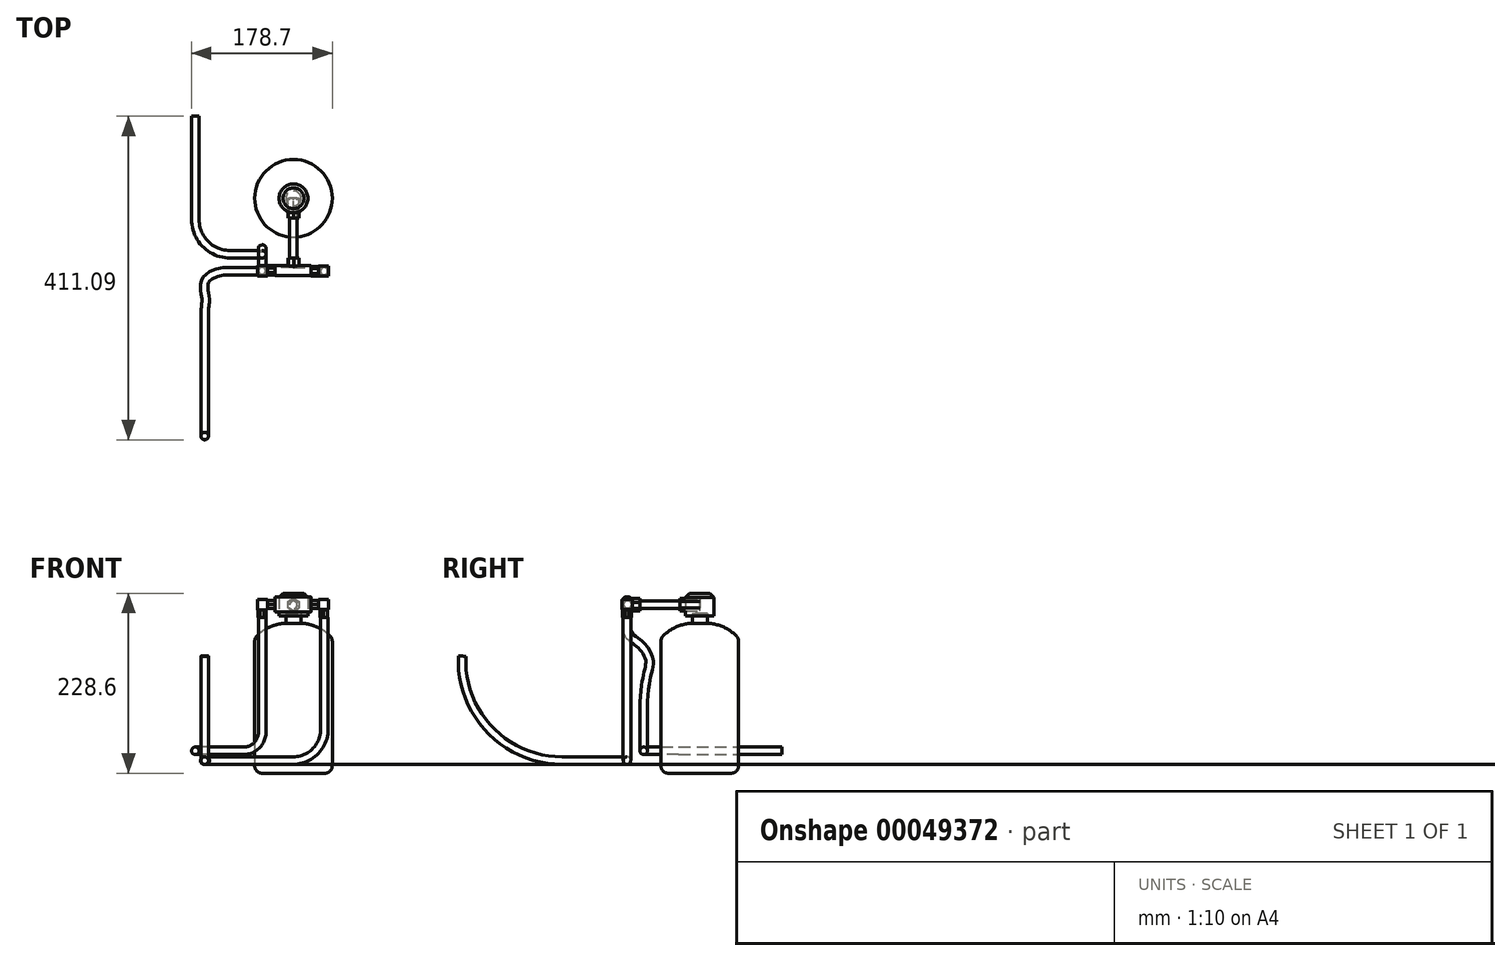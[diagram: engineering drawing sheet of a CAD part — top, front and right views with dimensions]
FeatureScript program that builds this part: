
annotation { "Feature Type Name" : "Feature", "Feature Type Description" : "" }
export const myFeature = defineFeature(function(context is Context, id is Id, definition is map)
    precondition{}
    {
        {
            var Q0;
            Q0=qCreatedBy(makeId("Front.planeOp"),FACE);
            var sketch = newSketch(context, id + "F0", { "sketchPlane" : qUnion([Q0])});
            skLineSegment(sketch, "E0", {"start": v(0, 0) * mm, "end": v(-49.28, 0) * mm});
            skLineSegment(sketch, "E1", {"start": v(-49.28, 0) * mm, "end": v(-49.28, 171.45) * mm});
            skArc(sketch, "E2", {"start": v(-9.53, 190.5) * mm, "mid": v(-31.43, 185.22) * mm, "end": v(-49.28, 171.45) * mm});
            skLineSegment(sketch, "E3.top", {"start": v(-9.53, 203.2) * mm, "end": v(0, 203.2) * mm});
            skLineSegment(sketch, "E3.left", {"start": v(-9.53, 190.5) * mm, "end": v(-9.53, 203.2) * mm});
            skLineSegment(sketch, "E4", {"start": v(0, 0) * mm, "end": v(0, 203.2) * mm});
            skSolve(sketch);
        }
        {
            var Q0;
            Q0 = qSketchRegion(id + "F0", true);
            var Q1;
            Q1=sQuery(id+"F0.wireOp",EDGE,"E4");
            revolve(context, id + "F1", {"entities" : qUnion([Q0]), "axis" : qUnion([Q1]), "revolveType" : RevolveType.FULL});
        }
        {
            var Q0;
            Q0=makeQuery(id+"F1.opRevolve","SWEPT_EDGE",EDGE,{"disambiguationData":[OSD([sQuery(id+"F0.wireOp",EDGE,"E1"),sQuery(id+"F0.wireOp",EDGE,"E2")])]});
            var Q1;
            Q1=makeQuery(id+"F1.opRevolve","SWEPT_EDGE",EDGE,{"disambiguationData":[OSD([sQuery(id+"F0.wireOp",EDGE,"E0"),sQuery(id+"F0.wireOp",EDGE,"E1")])]});
            fillet(context, id + "F2", {"entities" : qUnion([Q0, Q1]), "radius" : 9.52 * mm, "tangentPropagation" : true, "allowEdgeOverflow" : false});
        }
        {
            var Q0;
            Q0=makeQuery(id+"F1.opRevolve","SWEPT_FACE",FACE,{"disambiguationData":[OSD([sQuery(id+"F0.wireOp",EDGE,"E3.top")])]});
            var sketch = newSketch(context, id + "F3", { "sketchPlane" : qUnion([Q0])});
            skCircle(sketch, "E5", {"center": v(0, 0) * mm, "radius": 18.26 * mm});
            skSolve(sketch);
        }
        {
            var Q0;
            Q0 = qSketchRegion(id + "F3", true);
            extrude(context, id + "F4", {"entities" : qUnion([Q0]), "depth" : 25.4 * mm, "hasSecondDirection" : true, "secondDirectionOppositeDirection" : true, "secondDirectionDepth" : 3.17 * mm});
        }
        {
            var Q0;
            Q0=qCreatedBy(makeId("Front.planeOp"),FACE);
            var sketch = newSketch(context, id + "F5", { "sketchPlane" : qUnion([Q0])});
            skCircle(sketch, "E6", {"center": v(0, 213.92) * mm, "radius": 4.76 * mm});
            skSolve(sketch);
        }
        {
            var Q0;
            Q0 = qSketchRegion(id + "F5", true);
            extrude(context, id + "F6", {"entities" : qUnion([Q0]), "depth" : 76.2 * mm});
        }
        {
            var Q0;
            Q0=qCreatedBy(makeId("Front.planeOp"),FACE);
            var sketch = newSketch(context, id + "F7", { "sketchPlane" : qUnion([Q0])});
            skCircle(sketch, "E7.cCircle", {"center": v(0, 214.17) * mm, "radius": 6.76 * mm, "construction": true});
            skLineSegment(sketch, "E7.0", {"start": v(6.76, 218.07) * mm, "end": v(6.76, 210.26) * mm});
            skLineSegment(sketch, "E7.1", {"start": v(6.76, 210.26) * mm, "end": v(0, 206.36) * mm});
            skLineSegment(sketch, "E7.2", {"start": v(0, 206.36) * mm, "end": v(-6.76, 210.26) * mm});
            skLineSegment(sketch, "E7.3", {"start": v(-6.76, 210.26) * mm, "end": v(-6.76, 218.07) * mm});
            skLineSegment(sketch, "E7.4", {"start": v(-6.76, 218.07) * mm, "end": v(0, 221.97) * mm});
            skLineSegment(sketch, "E7.5", {"start": v(0, 221.97) * mm, "end": v(6.76, 218.07) * mm});
            skPoint(sketch, "E7.0.midPoint", {"position": v(6.76, 214.17) * mm});
            skSolve(sketch);
        }
        {
            var Q0;
            Q0 = qSketchRegion(id + "F7", true);
            extrude(context, id + "F8", {"entities" : qUnion([Q0]), "depth" : 25.4 * mm});
        }
        {
            var Q0;
            Q0=makeQuery(id+"F4.opExtrude","CAP_EDGE",EDGE,{"disambiguationData":[OSD([sQuery(id+"F3.wireOp",EDGE,"E5")])],"isStart":false});
            chamfer(context, id + "F9", {"entities" : qUnion([Q0]), "width" : 5.08 * mm, "tangentPropagation" : true});
        }
        {
            var Q0;
            Q0=makeQuery(id+"F6.opExtrude","CAP_FACE",FACE,{"disambiguationData":[OSD([sQuery(id+"F5.wireOp",EDGE,"E6")])],"isStart":false});
            var sketch = newSketch(context, id + "F10", { "sketchPlane" : qUnion([Q0])});
            skCircle(sketch, "E8.cCircle", {"center": v(0, 213.92) * mm, "radius": 6.92 * mm, "construction": true});
            skLineSegment(sketch, "E8.0", {"start": v(-6.54, 218.5) * mm, "end": v(0.7, 221.87) * mm});
            skLineSegment(sketch, "E8.1", {"start": v(0.7, 221.87) * mm, "end": v(7.24, 217.3) * mm});
            skLineSegment(sketch, "E8.2", {"start": v(7.24, 217.3) * mm, "end": v(6.54, 209.34) * mm});
            skLineSegment(sketch, "E8.3", {"start": v(6.54, 209.34) * mm, "end": v(-0.7, 205.96) * mm});
            skLineSegment(sketch, "E8.4", {"start": v(-0.7, 205.96) * mm, "end": v(-7.24, 210.54) * mm});
            skLineSegment(sketch, "E8.5", {"start": v(-7.24, 210.54) * mm, "end": v(-6.54, 218.5) * mm});
            skPoint(sketch, "E8.0.midPoint", {"position": v(-2.92, 220.19) * mm});
            skSolve(sketch);
        }
        {
            var Q0;
            Q0 = qSketchRegion(id + "F10", true);
            extrude(context, id + "F11", {"entities" : qUnion([Q0]), "depth" : 9.52 * mm});
        }
        {
            var Q0;
            Q0=makeQuery(id+"F11.opExtrude","CAP_FACE",FACE,{"disambiguationData":[OSD([sQuery(id+"F10.wireOp",EDGE,"E8.0"),sQuery(id+"F10.wireOp",EDGE,"E8.1"),sQuery(id+"F10.wireOp",EDGE,"E8.2"),sQuery(id+"F10.wireOp",EDGE,"E8.3"),sQuery(id+"F10.wireOp",EDGE,"E8.4"),sQuery(id+"F10.wireOp",EDGE,"E8.5")])],"isStart":false});
            var sketch = newSketch(context, id + "F12", { "sketchPlane" : qUnion([Q0])});
            skLineSegment(sketch, "E9.bottom", {"start": v(-23.42, 223.95) * mm, "end": v(22.3, 223.95) * mm});
            skLineSegment(sketch, "E9.top", {"start": v(-23.42, 205) * mm, "end": v(22.3, 205) * mm});
            skLineSegment(sketch, "E9.left", {"start": v(-23.42, 223.95) * mm, "end": v(-23.42, 205) * mm});
            skLineSegment(sketch, "E9.right", {"start": v(22.3, 223.95) * mm, "end": v(22.3, 205) * mm});
            skSolve(sketch);
        }
        {
            var Q0;
            Q0 = qSketchRegion(id + "F12", true);
            extrude(context, id + "F13", {"entities" : qUnion([Q0]), "operationType" : NewBodyOperationType.ADD, "depth" : 12.7 * mm});
        }
        {
            var Q0;
            Q0=makeQuery(id+"F13.opExtrude","SWEPT_FACE",FACE,{"disambiguationData":[OSD([sQuery(id+"F12.wireOp",EDGE,"E9.right")])]});
            var sketch = newSketch(context, id + "F14", { "sketchPlane" : qUnion([Q0])});
            skCircle(sketch, "E10.cCircle", {"center": v(-92.54, 214.36) * mm, "radius": 5.27 * mm, "construction": true});
            skLineSegment(sketch, "E10.0", {"start": v(-95.58, 219.63) * mm, "end": v(-89.5, 219.63) * mm});
            skLineSegment(sketch, "E10.1", {"start": v(-89.5, 219.63) * mm, "end": v(-86.46, 214.36) * mm});
            skLineSegment(sketch, "E10.2", {"start": v(-86.46, 214.36) * mm, "end": v(-89.5, 209.1) * mm});
            skLineSegment(sketch, "E10.3", {"start": v(-89.5, 209.1) * mm, "end": v(-95.58, 209.1) * mm});
            skLineSegment(sketch, "E10.4", {"start": v(-95.58, 209.1) * mm, "end": v(-98.62, 214.36) * mm});
            skLineSegment(sketch, "E10.5", {"start": v(-98.62, 214.36) * mm, "end": v(-95.58, 219.63) * mm});
            skPoint(sketch, "E10.0.midPoint", {"position": v(-92.54, 219.63) * mm});
            skSolve(sketch);
        }
        {
            var Q0;
            Q0 = qSketchRegion(id + "F14", true);
            extrude(context, id + "F15", {"entities" : qUnion([Q0]), "operationType" : NewBodyOperationType.ADD, "depth" : 9.52 * mm});
        }
        {
            var Q0;
            Q0=makeQuery(id+"F13.opExtrude","SWEPT_FACE",FACE,{"disambiguationData":[OSD([sQuery(id+"F12.wireOp",EDGE,"E9.left")])]});
            var sketch = newSketch(context, id + "F16", { "sketchPlane" : qUnion([Q0])});
            skCircle(sketch, "E11.cCircle", {"center": v(91.5, 214.48) * mm, "radius": 5.26 * mm, "construction": true});
            skPoint(sketch, "E11.cCircle.centerSnap0", {"position": v(98.43, 214.48) * mm});
            skLineSegment(sketch, "E11.0", {"start": v(88.46, 219.74) * mm, "end": v(94.54, 219.74) * mm});
            skLineSegment(sketch, "E11.1", {"start": v(94.54, 219.74) * mm, "end": v(97.58, 214.48) * mm});
            skLineSegment(sketch, "E11.2", {"start": v(97.58, 214.48) * mm, "end": v(94.54, 209.21) * mm});
            skLineSegment(sketch, "E11.3", {"start": v(94.54, 209.21) * mm, "end": v(88.46, 209.21) * mm});
            skLineSegment(sketch, "E11.4", {"start": v(88.46, 209.21) * mm, "end": v(85.42, 214.48) * mm});
            skLineSegment(sketch, "E11.5", {"start": v(85.42, 214.48) * mm, "end": v(88.46, 219.74) * mm});
            skPoint(sketch, "E11.0.midPoint", {"position": v(91.5, 219.74) * mm});
            skSolve(sketch);
        }
        {
            var Q0;
            Q0 = qSketchRegion(id + "F16", true);
            extrude(context, id + "F17", {"entities" : qUnion([Q0]), "operationType" : NewBodyOperationType.ADD, "depth" : 9.52 * mm});
        }
        {
            var Q0;
            Q0=makeQuery(id+"F13.opExtrude","CAP_EDGE",EDGE,{"disambiguationData":[OSD([sQuery(id+"F12.wireOp",EDGE,"E9.bottom")])],"isStart":false});
            var Q1;
            Q1=makeQuery(id+"F13.opExtrude","CAP_EDGE",EDGE,{"disambiguationData":[OSD([sQuery(id+"F12.wireOp",EDGE,"E9.top")])],"isStart":false});
            var Q2;
            Q2=makeQuery(id+"F13.opExtrude","CAP_EDGE",EDGE,{"disambiguationData":[OSD([sQuery(id+"F12.wireOp",EDGE,"E9.bottom")])],"isStart":true});
            var Q3;
            Q3=makeQuery(id+"F13.opExtrude","CAP_EDGE",EDGE,{"disambiguationData":[OSD([sQuery(id+"F12.wireOp",EDGE,"E9.top")])],"isStart":true});
            fillet(context, id + "F18", {"entities" : qUnion([Q0, Q1, Q2, Q3]), "radius" : 5.08 * mm, "tangentPropagation" : true, "allowEdgeOverflow" : false});
        }
        {
            var Q0;
            Q0=makeQuery(id+"F17.opExtrude","CAP_FACE",FACE,{"disambiguationData":[OSD([sQuery(id+"F16.wireOp",EDGE,"E11.0"),sQuery(id+"F16.wireOp",EDGE,"E11.1"),sQuery(id+"F16.wireOp",EDGE,"E11.2"),sQuery(id+"F16.wireOp",EDGE,"E11.3"),sQuery(id+"F16.wireOp",EDGE,"E11.4"),sQuery(id+"F16.wireOp",EDGE,"E11.5")])],"isStart":false});
            var sketch = newSketch(context, id + "F19", { "sketchPlane" : qUnion([Q0])});
            skLineSegment(sketch, "E12.bottom", {"start": v(85.42, 207.7) * mm, "end": v(98.52, 207.7) * mm});
            skLineSegment(sketch, "E12.top", {"start": v(85.42, 220.8) * mm, "end": v(98.52, 220.8) * mm});
            skLineSegment(sketch, "E12.left", {"start": v(85.42, 207.7) * mm, "end": v(85.42, 220.8) * mm});
            skLineSegment(sketch, "E12.right", {"start": v(98.52, 207.7) * mm, "end": v(98.52, 220.8) * mm});
            skSolve(sketch);
        }
        {
            var Q0;
            Q0 = qSketchRegion(id + "F19", true);
            extrude(context, id + "F20", {"entities" : qUnion([Q0]), "operationType" : NewBodyOperationType.ADD, "depth" : 12.7 * mm});
        }
        {
            var Q0;
            Q0=makeQuery(id+"F15.opExtrude","CAP_FACE",FACE,{"disambiguationData":[OSD([sQuery(id+"F14.wireOp",EDGE,"E10.0"),sQuery(id+"F14.wireOp",EDGE,"E10.1"),sQuery(id+"F14.wireOp",EDGE,"E10.2"),sQuery(id+"F14.wireOp",EDGE,"E10.3"),sQuery(id+"F14.wireOp",EDGE,"E10.4"),sQuery(id+"F14.wireOp",EDGE,"E10.5")])],"isStart":false});
            var sketch = newSketch(context, id + "F21", { "sketchPlane" : qUnion([Q0])});
            skLineSegment(sketch, "E13.bottom", {"start": v(-98.83, 221) * mm, "end": v(-85.73, 221) * mm});
            skLineSegment(sketch, "E13.top", {"start": v(-98.83, 207.9) * mm, "end": v(-85.73, 207.9) * mm});
            skLineSegment(sketch, "E13.left", {"start": v(-98.83, 221) * mm, "end": v(-98.83, 207.9) * mm});
            skLineSegment(sketch, "E13.right", {"start": v(-85.73, 221) * mm, "end": v(-85.73, 207.9) * mm});
            skSolve(sketch);
        }
        {
            var Q0;
            Q0 = qSketchRegion(id + "F21", true);
            extrude(context, id + "F22", {"entities" : qUnion([Q0]), "operationType" : NewBodyOperationType.ADD, "depth" : 12.7 * mm});
        }
        {
            var Q0;
            Q0=makeQuery(id+"F20.opExtrude","SWEPT_FACE",FACE,{"disambiguationData":[OSD([sQuery(id+"F19.wireOp",EDGE,"E12.bottom")])]});
            var sketch = newSketch(context, id + "F23", { "sketchPlane" : qUnion([Q0])});
            skCircle(sketch, "E14.cCircle", {"center": v(-40.15, 91.97) * mm, "radius": 4.4 * mm, "construction": true});
            skPoint(sketch, "E14.cCircle.centerSnap0", {"position": v(-45.64, 91.97) * mm});
            skLineSegment(sketch, "E14.0", {"start": v(-42.68, 96.36) * mm, "end": v(-37.61, 96.36) * mm});
            skLineSegment(sketch, "E14.1", {"start": v(-37.61, 96.36) * mm, "end": v(-35.07, 91.97) * mm});
            skLineSegment(sketch, "E14.2", {"start": v(-35.07, 91.97) * mm, "end": v(-37.61, 87.58) * mm});
            skLineSegment(sketch, "E14.3", {"start": v(-37.61, 87.58) * mm, "end": v(-42.68, 87.58) * mm});
            skLineSegment(sketch, "E14.4", {"start": v(-42.68, 87.58) * mm, "end": v(-45.22, 91.97) * mm});
            skLineSegment(sketch, "E14.5", {"start": v(-45.22, 91.97) * mm, "end": v(-42.68, 96.36) * mm});
            skPoint(sketch, "E14.0.midPoint", {"position": v(-40.15, 96.36) * mm});
            skCircle(sketch, "E15.cCircle", {"center": v(38.36, 92.5) * mm, "radius": 4.76 * mm, "construction": true});
            skLineSegment(sketch, "E15.0", {"start": v(33.6, 89.75) * mm, "end": v(33.6, 95.25) * mm});
            skLineSegment(sketch, "E15.1", {"start": v(33.6, 95.25) * mm, "end": v(38.36, 98) * mm});
            skLineSegment(sketch, "E15.2", {"start": v(38.36, 98) * mm, "end": v(43.12, 95.25) * mm});
            skLineSegment(sketch, "E15.3", {"start": v(43.12, 95.25) * mm, "end": v(43.12, 89.75) * mm});
            skLineSegment(sketch, "E15.4", {"start": v(43.12, 89.75) * mm, "end": v(38.36, 87) * mm});
            skLineSegment(sketch, "E15.5", {"start": v(38.36, 87) * mm, "end": v(33.6, 89.75) * mm});
            skPoint(sketch, "E15.0.midPoint", {"position": v(33.6, 92.5) * mm});
            skSolve(sketch);
        }
        {
            var Q0;
            Q0 = qSketchRegion(id + "F23", true);
            extrude(context, id + "F24", {"entities" : qUnion([Q0]), "depth" : 9.52 * mm});
        }
        {
            var Q0;
            Q0=makeQuery(id+"F22.opExtrude","SWEPT_FACE",FACE,{"disambiguationData":[OSD([sQuery(id+"F21.wireOp",EDGE,"E13.left")])]});
            cPlane(context, id + "F25", {"entities" : qUnion([Q0]), "cplaneType" : CPlaneType.OFFSET, "offset" : 6.35 * mm, "oppositeDirection" : true, "width" : 152.4 * mm, "height" : 152.4 * mm});
        }
        {
            var Q0;
            Q0=qCreatedBy(id+"F25.planeOp",FACE);
            var sketch = newSketch(context, id + "F26", { "sketchPlane" : qUnion([Q0])});
            skLineSegment(sketch, "E16", {"start": v(-39.68, 198.17) * mm, "end": v(-39.68, 147.37) * mm, "construction": true});
            skLineSegment(sketch, "E17", {"start": v(39.21, 198.17) * mm, "end": v(39.21, 147.37) * mm, "construction": true});
            skSolve(sketch);
        }
        {
            var Q0;
            Q0=sQuery(id+"F26.wireOp",EDGE,"E16");
            cPlane(context, id + "F27", {"entities" : qUnion([Q0]), "cplaneType" : CPlaneType.LINE_ANGLE, "offset" : 152.4 * mm, "angle" : 0 * degree, "width" : 152.4 * mm, "height" : 152.4 * mm});
        }
        {
            var Q0;
            Q0=sQuery(id+"F26.wireOp",EDGE,"E17");
            cPlane(context, id + "F28", {"entities" : qUnion([Q0]), "cplaneType" : CPlaneType.LINE_ANGLE, "offset" : 152.4 * mm, "angle" : 0 * degree, "width" : 152.4 * mm, "height" : 152.4 * mm});
        }
        {
            var Q0;
            Q0=qCreatedBy(id+"F27.planeOp",FACE);
            var sketch = newSketch(context, id + "F29", { "sketchPlane" : qUnion([Q0])});
            skFitSpline(sketch, "E18", {"points": [v(92.48, 185.83) * mm, v(79.84, 166.81) * mm, v(64.2, 145.8) * mm, v(71.16, 83.45) * mm], "startDerivative": vector(0, -135.64) * mm, "endDerivative": vector(0, -266.86) * mm});
            skLineSegment(sketch, "E19", {"start": v(92.48, 185.83) * mm, "end": v(92.48, 198.17) * mm});
            skLineSegment(sketch, "E20", {"start": v(71.16, 83.45) * mm, "end": v(71.16, 59.44) * mm});
            skSolve(sketch);
        }
        {
            var Q0;
            Q0=sQuery(id+"F29.wireOp",EDGE,"E20");
            cPlane(context, id + "F30", {"entities" : qUnion([Q0]), "cplaneType" : CPlaneType.LINE_ANGLE, "offset" : 152.4 * mm, "angle" : 90 * degree, "width" : 152.4 * mm, "height" : 152.4 * mm});
        }
        {
            var Q0;
            Q0=qCreatedBy(id+"F30.planeOp",FACE);
            var sketch = newSketch(context, id + "F31", { "sketchPlane" : qUnion([Q0])});
            skLineSegment(sketch, "E21", {"start": v(39.68, 59.44) * mm, "end": v(39.68, 52.43) * mm});
            skArc(sketch, "E22", {"start": v(39.68, 52.43) * mm, "mid": v(46.67, 35.55) * mm, "end": v(63.56, 28.55) * mm});
            skLineSegment(sketch, "E23", {"start": v(63.56, 28.55) * mm, "end": v(80.36, 28.55) * mm});
            skSolve(sketch);
        }
        {
            var Q0;
            Q0=makeQuery(id+"F24.opExtrude","CAP_FACE",FACE,{"disambiguationData":[OSD([sQuery(id+"F23.wireOp",EDGE,"E14.0"),sQuery(id+"F23.wireOp",EDGE,"E14.1"),sQuery(id+"F23.wireOp",EDGE,"E14.2"),sQuery(id+"F23.wireOp",EDGE,"E14.3"),sQuery(id+"F23.wireOp",EDGE,"E14.4"),sQuery(id+"F23.wireOp",EDGE,"E14.5")])],"isStart":false});
            var sketch = newSketch(context, id + "F32", { "sketchPlane" : qUnion([Q0])});
            skCircle(sketch, "E24", {"center": v(-39.68, 92.48) * mm, "radius": 4.76 * mm});
            skSolve(sketch);
        }
        {
            var Q0;
            Q0=qCreatedBy(id+"F28.planeOp",FACE);
            var sketch = newSketch(context, id + "F33", { "sketchPlane" : qUnion([Q0])});
            skLineSegment(sketch, "E25", {"start": v(92.5, 198.17) * mm, "end": v(92.5, 55.89) * mm});
            skSolve(sketch);
        }
        {
            var Q0;
            Q0=sQuery(id+"F33.wireOp",EDGE,"E25");
            cPlane(context, id + "F34", {"entities" : qUnion([Q0]), "cplaneType" : CPlaneType.LINE_ANGLE, "offset" : 152.4 * mm, "angle" : 90 * degree, "width" : 152.4 * mm, "height" : 152.4 * mm});
        }
        {
            var Q0;
            Q0=qCreatedBy(id+"F34.planeOp",FACE);
            var sketch = newSketch(context, id + "F35", { "sketchPlane" : qUnion([Q0])});
            skArc(sketch, "E26", {"start": v(-39.21, 55.89) * mm, "mid": v(-27.56, 27.75) * mm, "end": v(0.58, 16.1) * mm});
            skLineSegment(sketch, "E27", {"start": v(0.58, 16.1) * mm, "end": v(62.14, 16.1) * mm});
            skSolve(sketch);
        }
        {
            var Q0;
            Q0=sQuery(id+"F35.wireOp",EDGE,"E27");
            cPlane(context, id + "F36", {"entities" : qUnion([Q0]), "cplaneType" : CPlaneType.LINE_ANGLE, "offset" : 152.4 * mm, "angle" : 90 * degree, "width" : 152.4 * mm, "height" : 152.4 * mm});
        }
        {
            var Q0;
            Q0=qCreatedBy(id+"F36.planeOp",FACE);
            var sketch = newSketch(context, id + "F37", { "sketchPlane" : qUnion([Q0])});
            skLineSegment(sketch, "E28", {"start": v(-62.14, -92.5) * mm, "end": v(-80.77, -92.5) * mm});
            skFitSpline(sketch, "E29", {"points": [v(-80.77, -92.5) * mm, v(-112.41, -105.98) * mm, v(-111.67, -126.63) * mm, v(-112.7, -141.75) * mm, v(-112.82, -157.86) * mm], "startDerivative": vector(-157.24, 0) * mm, "endDerivative": vector(0, -117.63) * mm});
            skLineSegment(sketch, "E30", {"start": v(-112.82, -157.86) * mm, "end": v(-112.82, -175.06) * mm});
            skSolve(sketch);
        }
        {
            var Q0;
            Q0=makeQuery(id+"F24.opExtrude","CAP_FACE",FACE,{"disambiguationData":[OSD([sQuery(id+"F23.wireOp",EDGE,"E15.0"),sQuery(id+"F23.wireOp",EDGE,"E15.1"),sQuery(id+"F23.wireOp",EDGE,"E15.2"),sQuery(id+"F23.wireOp",EDGE,"E15.3"),sQuery(id+"F23.wireOp",EDGE,"E15.4"),sQuery(id+"F23.wireOp",EDGE,"E15.5")])],"isStart":false});
            var sketch = newSketch(context, id + "F38", { "sketchPlane" : qUnion([Q0])});
            skCircle(sketch, "E31", {"center": v(39.21, 92.5) * mm, "radius": 4.76 * mm});
            skSolve(sketch);
        }
        {
            var Q0;
            Q0=sQuery(id+"F37.wireOp",EDGE,"E30");
            cPlane(context, id + "F39", {"entities" : qUnion([Q0]), "cplaneType" : CPlaneType.LINE_ANGLE, "offset" : 152.4 * mm, "angle" : 90 * degree, "width" : 152.4 * mm, "height" : 152.4 * mm});
        }
        {
            var Q0;
            Q0=qCreatedBy(id+"F39.planeOp",FACE);
            var sketch = newSketch(context, id + "F40", { "sketchPlane" : qUnion([Q0])});
            skArc(sketch, "E32", {"start": v(-301.93, 148.81) * mm, "mid": v(-266.86, 55.34) * mm, "end": v(-175.06, 16.1) * mm});
            skSolve(sketch);
        }
        {
            var Q0;
            Q0 = qSketchRegion(id + "F38", true);
            var Q1;
            Q1=sQuery(id+"F33.wireOp",EDGE,"E25");
            var Q2;
            Q2=sQuery(id+"F35.wireOp",EDGE,"E26");
            var Q3;
            Q3=sQuery(id+"F35.wireOp",EDGE,"E27");
            var Q4;
            Q4=sQuery(id+"F37.wireOp",EDGE,"E28");
            var Q5;
            Q5=sQuery(id+"F37.wireOp",EDGE,"E29");
            var Q6;
            Q6=sQuery(id+"F37.wireOp",EDGE,"E30");
            var Q7;
            Q7=sQuery(id+"F40.wireOp",EDGE,"E32");
            sweep(context, id + "F41", {"operationType" : NewBodyOperationType.ADD, "profiles" : qUnion([Q0]), "path" : qUnion([Q1, Q2, Q3, Q4, Q5, Q6, Q7])});
        }
        {
            var Q0;
            Q0=sQuery(id+"F31.wireOp",EDGE,"E23");
            cPlane(context, id + "F42", {"entities" : qUnion([Q0]), "cplaneType" : CPlaneType.LINE_ANGLE, "offset" : 152.4 * mm, "angle" : 90 * degree, "width" : 152.4 * mm, "height" : 152.4 * mm});
        }
        {
            var Q0;
            Q0=qCreatedBy(id+"F42.planeOp",FACE);
            var sketch = newSketch(context, id + "F43", { "sketchPlane" : qUnion([Q0])});
            skArc(sketch, "E33", {"start": v(-124.65, -26.86) * mm, "mid": v(-111.68, -58.18) * mm, "end": v(-80.36, -71.16) * mm});
            skLineSegment(sketch, "E34", {"start": v(-124.65, -26.86) * mm, "end": v(-124.65, 104.27) * mm});
            skSolve(sketch);
        }
        {
            var Q0;
            Q0 = qSketchRegion(id + "F32", true);
            var Q1;
            Q1=sQuery(id+"F29.wireOp",EDGE,"E19");
            var Q2;
            Q2=sQuery(id+"F29.wireOp",EDGE,"E18");
            var Q3;
            Q3=sQuery(id+"F29.wireOp",EDGE,"E20");
            var Q4;
            Q4=sQuery(id+"F31.wireOp",EDGE,"E22");
            var Q5;
            Q5=sQuery(id+"F31.wireOp",EDGE,"E21");
            var Q6;
            Q6=sQuery(id+"F31.wireOp",EDGE,"E23");
            var Q7;
            Q7=sQuery(id+"F43.wireOp",EDGE,"E33");
            var Q8;
            Q8=sQuery(id+"F43.wireOp",EDGE,"E34");
            sweep(context, id + "F44", {"operationType" : NewBodyOperationType.ADD, "profiles" : qUnion([Q0]), "path" : qUnion([Q1, Q2, Q3, Q4, Q5, Q6, Q7, Q8])});
        }
    });
